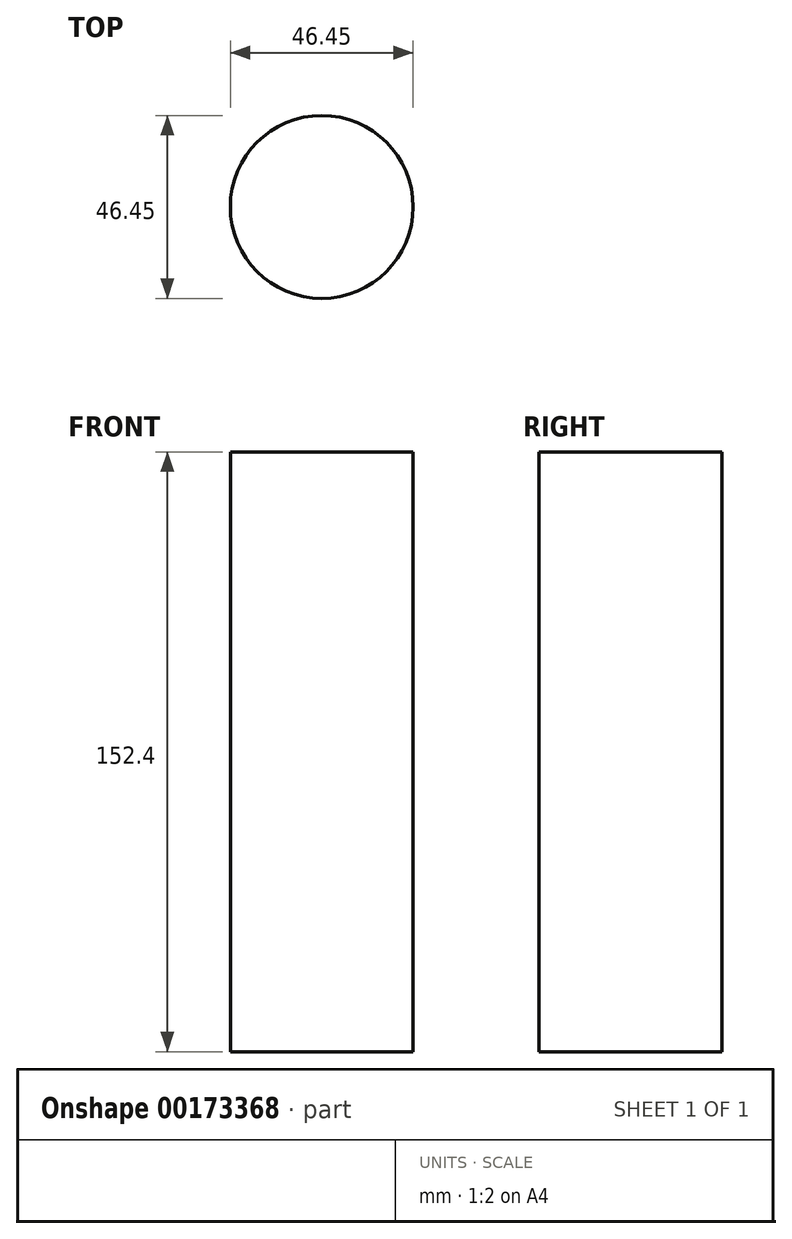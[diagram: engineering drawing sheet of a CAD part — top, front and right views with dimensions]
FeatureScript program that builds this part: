
annotation { "Feature Type Name" : "Feature", "Feature Type Description" : "" }
export const myFeature = defineFeature(function(context is Context, id is Id, definition is map)
    precondition{}
    {
        {
            var Q0;
            Q0=qCreatedBy(makeId("Top.planeOp"),FACE);
            var sketch = newSketch(context, id + "F0", { "sketchPlane" : qUnion([Q0])});
            skCircle(sketch, "E0", {"center": v(-19.3, 12.93) * mm, "radius": 23.22 * mm});
            skPoint(sketch, "E0.first.point", {"position": v(0, 0) * mm});
            skPoint(sketch, "E0.second.point", {"position": v(-35.64, 29.42) * mm});
            skPoint(sketch, "E0.third.point", {"position": v(-4.67, 30.97) * mm});
            skSolve(sketch);
        }
        {
            var Q0;
            Q0=makeQuery(id+"F0.imprint","IMPRINT",FACE,{"disambiguationData":[TD([[makeQuery(id+"F0.imprint","IMPRINT",EDGE,{"derivedFrom":sQuery(id+"F0.wireOp",EDGE,"E0")}),1.0]])]});
            extrude(context, id + "F1", {"entities" : qUnion([Q0]), "endBound" : BoundingType.SYMMETRIC, "depth" : 152.4 * mm});
        }
    });
